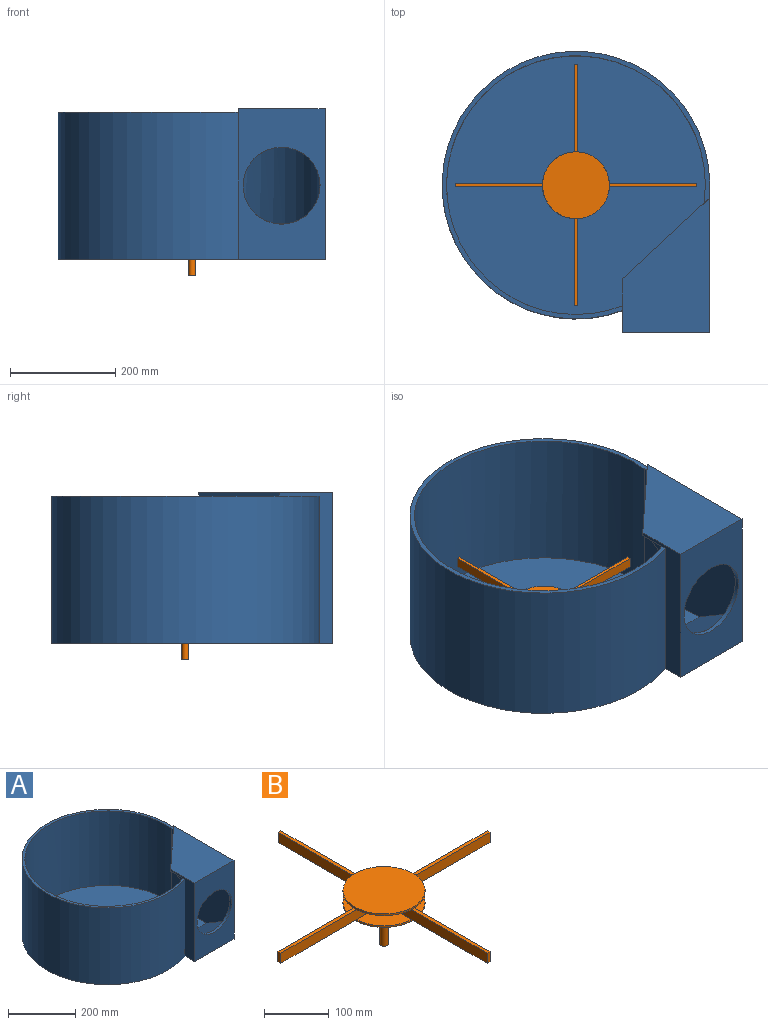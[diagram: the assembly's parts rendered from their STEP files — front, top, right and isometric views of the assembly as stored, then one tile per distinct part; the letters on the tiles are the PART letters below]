
ASSEMBLY  parts=2 mates=1
PART A: 20 faces, bbox 508x533.4x285.8 mm
  f0: plane 271.02x148.34mm, normal (0,1,0), area 5075.8mm2, adj f1,f9,f10,f11,f12,f13,f14,f15
  f1: plane 271.02x246.04mm, normal (-1,0,0), area 60728mm2, adj f0,f6,f8,f10,f12,f14,f18
  f2: cylinder r=254mm len=508mm, axis (0,0,-1), area 366532.2mm2, adj f3,f5,f6,f7
  f3: plane 285.75x101.31mm, normal (-1,0,0), area 12097mm2, adj f2,f4,f6,f7,f16,f17,f18
  f4: plane 285.75x165.1mm, normal (0,-1,0), area 30424.3mm2, adj f3,f5,f7,f11,f17
  f5: plane 285.75x254mm, normal (1,0,0), area 72580.5mm2, adj f2,f4,f7,f16,f17
  f6: plane 508x508mm, normal (0,0,1), area 10863.5mm2, adj f1,f2,f3,f8,f16
  f7: plane 533.4x508mm, normal (0,0,-1), area 219843.6mm2, adj f2,f3,f4,f5,f19
  f8: cylinder r=245.62mm len=491.24mm, axis (0,0,-1), area 347202.8mm2, adj f1,f6,f9,f10,f18
  f9: plane 271.02x44.94mm, normal (1,0,0), area 12180mm2, adj f0,f8,f10,f18
  f10: plane 516.64x491.24mm, normal (0,0,1), area 190712.4mm2, adj f0,f1,f8,f9,f12,f13,f19
  f11: cylinder r=73.03mm len=146.05mm, axis (0,-1,0), area 3845.9mm2, adj f0,f4
  f12: plane 147.32x98.39mm, normal (0,0.51,0.86), area 16838.7mm2, adj f0,f1,f10,f13
  f13: plane 98.39x58.17mm, normal (-1,0,0), area 2861.6mm2, adj f0,f10,f12
  f14: plane 147.32x92.93mm, normal (0,0.58,-0.81), area 16838.7mm2, adj f0,f1,f15,f18
  f15: plane 92.93x66.55mm, normal (-1,0,0), area 3092.1mm2, adj f0,f14,f18
  f16: plane 165.1x152.69mm, normal (-0.68,0.73,0), area 1428mm2, adj f3,f5,f6,f17,f18
  f17: plane 254x165.1mm, normal (0,0,1), area 29330.9mm2, adj f3,f4,f5,f16
  f18: plane 237.87x156.72mm, normal (0,0,-1), area 11868.2mm2, adj f0,f1,f3,f8,f9,f14,f15,f16
  f19: cylinder r=6.35mm len=12.7mm, axis (0,0,1), area 334.4mm2, adj f7,f10
PART B: 32 faces, bbox 457.2x457.2x101.6 mm
  f0: plane 126.84x126.84mm, normal (0,0,1), area 11700.6mm2, adj f3,f6,f7,f9,f11,f12,f13,f17
  f1: cylinder r=6.35mm len=76.2mm, axis (0,0,-1), area 3040.2mm2, adj f2,f4
  f2: plane 12.7x12.7mm, normal (0,0,-1), area 126.7mm2, adj f1
  f3: cylinder r=63.5mm len=127mm, axis (0,0,-1), area 1266.8mm2, adj f0,f4,f5,f16,f22,f28
  f4: plane 127x127mm, normal (0,0,-1), area 12541mm2, adj f1,f3
  f5: plane 165.18x6.35mm, normal (0,0,-1), area 1048.6mm2, adj f3,f7,f8,f9
  f6: plane 19.05x6.35mm, normal (0,-1,0), area 121mm2, adj f0,f7,f9,f29
  f7: plane 203.2x19.05mm, normal (1,0,0), area 3871mm2, adj f0,f5,f6,f8,f10,f29
  f8: plane 19.05x6.35mm, normal (0,1,0), area 121mm2, adj f5,f7,f9,f10
  f9: plane 203.2x19.05mm, normal (-1,0,0), area 3871mm2, adj f0,f5,f6,f8,f10,f29
  f10: plane 165.18x6.35mm, normal (0,0,1), area 1048.6mm2, adj f7,f8,f9,f30
  f11: plane 203.2x19.05mm, normal (0,-1,0), area 3871mm2, adj f0,f12,f14,f15,f16,f29
  f12: plane 19.05x6.35mm, normal (1,0,0), area 121mm2, adj f0,f11,f13,f29
  f13: plane 203.2x19.05mm, normal (0,1,0), area 3871mm2, adj f0,f12,f14,f15,f16,f29
  f14: plane 19.05x6.35mm, normal (-1,0,0), area 121mm2, adj f11,f13,f15,f16
  f15: plane 165.18x6.35mm, normal (0,0,1), area 1048.6mm2, adj f11,f13,f14,f30
  f16: plane 165.18x6.35mm, normal (0,0,-1), area 1048.6mm2, adj f3,f11,f13,f14
  f17: plane 203.2x19.05mm, normal (0,1,0), area 3871mm2, adj f0,f18,f20,f21,f22,f29
  f18: plane 19.05x6.35mm, normal (-1,0,0), area 121mm2, adj f0,f17,f19,f29
  f19: plane 203.2x19.05mm, normal (0,-1,0), area 3871mm2, adj f0,f18,f20,f21,f22,f29
  f20: plane 19.05x6.35mm, normal (1,0,0), area 121mm2, adj f17,f19,f21,f22
  f21: plane 165.18x6.35mm, normal (0,0,1), area 1048.6mm2, adj f17,f19,f20,f30
  f22: plane 165.18x6.35mm, normal (0,0,-1), area 1048.6mm2, adj f3,f17,f19,f20
  f23: plane 203.2x19.05mm, normal (1,0,0), area 3871mm2, adj f0,f24,f26,f27,f28,f29
  f24: plane 19.05x6.35mm, normal (0,1,0), area 121mm2, adj f0,f23,f25,f29
  f25: plane 203.2x19.05mm, normal (-1,0,0), area 3871mm2, adj f0,f24,f26,f27,f28,f29
  f26: plane 19.05x6.35mm, normal (0,-1,0), area 121mm2, adj f23,f25,f27,f28
  f27: plane 165.18x6.35mm, normal (0,0,1), area 1048.6mm2, adj f23,f25,f26,f30
  f28: plane 165.18x6.35mm, normal (0,0,-1), area 1048.6mm2, adj f3,f23,f25,f26
  f29: plane 126.84x126.84mm, normal (0,0,-1), area 11700.6mm2, adj f6,f7,f9,f11,f12,f13,f17,f18
  f30: cylinder r=63.5mm len=127mm, axis (0,0,-1), area 1266.8mm2, adj f10,f15,f21,f27,f29,f31
  f31: plane 127x127mm, normal (0,0,1), area 12667.7mm2, adj f30
PLACE A t=(-402.69,-182,-228.6)mm
PLACE B t=(-402.69,-182,-220.83)mm
MATE slider A.f2 <-> B.f1  axis (0,0,1) through (-402.69,-182,-220.21)mm
